# Revit family: Deca_Acabamento para registro de pressão ½'' e ¾'' com mecanismo ½ volta_Duna Clássica_4916.64.PQ
name_source: partatom
category: Plumbing Fixtures
units: mm (PartAtom-declared; Revit-internal decimal feet)

## family parameters
Cut with Voids When Loaded = No
Host = Face
Part Type = Normal
Room Calculation Point = No
Round Connector Dimension = Use Radius
Shared = No

## types (4) — shared parameters
Acompanha o Produto = -
Aprovado por = quattroD
Atendimento ao Cliente = 0800-0117073
Categoria = METAIS PARA BANHEIRO
Composição Anel Vedação = -
Composição Assento = -
Composição Básica = Liga de Cobre (bronze e latão),Plásticos de Engenharia,Elastômeros
Composição Componente = -
Consumo = -
Cor Interna = -
Cor Secundária = -
Cores Componente = -
Criado por = quattroD
Código Pai = 4916.64.PQ
Default Elevation = 1100 mm
Description = Acabamento para registro de pressão 1/2" e 3/4" com mecanismo 1/2 volta
Informações Complementares = -
Itens de Instalação = -
Linha = Duna Classica
Manufacturer = Deca
Norma = Não Possui
Peso Líquido (Kg) = 0.643
Pressão máx. funcionamento = -
Pressão mín. Aquec. Acúmulo = -
Pressão mín. Aquec. Passagem = -
Pressão mín. funcionamento = -
Saída de Esgoto = -
Segmento = Banheiro Luxo
Tipo de dispositivo economizador = -
Tipo de mecanismo utilizado = MVR - 1/2 volta
Tipo de rosca de entrada = -
Tipo de rosca de saída = -
URL = www.deca.com.br
Vazão na Pressão máx. (L/min) = -
Vazão na Pressão mín. (L/min) = -
zero-valued in all types: CWFU

## per-type parameters (varying)
| type | Cor Principal | Material | Model |
| 4916.C64.PQ_Cromado | Cromado | Deca_Cromado | 4916.C64.PQ |
| 4916.CT64.PQ.MT_Corten | Corten | Deca_Corten | 4916.CT64.PQ.MT |
| 4916.GL64.PQ.RD_Red Gold | Red Gold | Deca_Red Gold | 4916.GL64.PQ.RD |
| 4916.BL64.PQ.MT_Black Matte | Black Matte | Deca_Black Matte | 4916.BL64.PQ.MT |

## geometry (parser evidence)
native form markers: Sweep x2
no freeform markers — native parametric forms only
